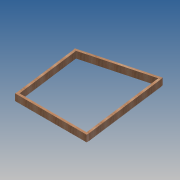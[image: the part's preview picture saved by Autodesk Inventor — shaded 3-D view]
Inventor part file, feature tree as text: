
AUTODESK INVENTOR PART (.ipt)
format: ipt  version: 2014 SP1 (Build 180222100, 222)  size: 116,736 bytes
history: native  units: in
note: dims shown in document units (in); Inventor stores cm internally (conversion verified against a paired STEP export)
features: extrude x3, sketch x3
ambient origin geometry x8: Origin, YZ Plane, XZ Plane, XY Plane, X Axis, Y Axis, Z Axis, Center Point
bodies: Body1 (feature_tree)
feature tree (6):
  extrude  "Extrusion2"  Depth=1.9685in
  extrude  "Extrusion3"  Depth=163.3858in
  extrude  "Extrusion4"  Depth=1.4961in
  sketch  "Sketch1"  dims[d0=165.0deg d3=1.9685in]
  sketch  "Sketch2"  dims[d4=1.9685in d6=163.3858in]
  sketch  "Sketch3"  dims[d7=1.1853in d10=1.4961in d11=4.4882in d12=0.0in d13=0.0394in d14=0.0in d15=0.0394in d16=0.0in]
